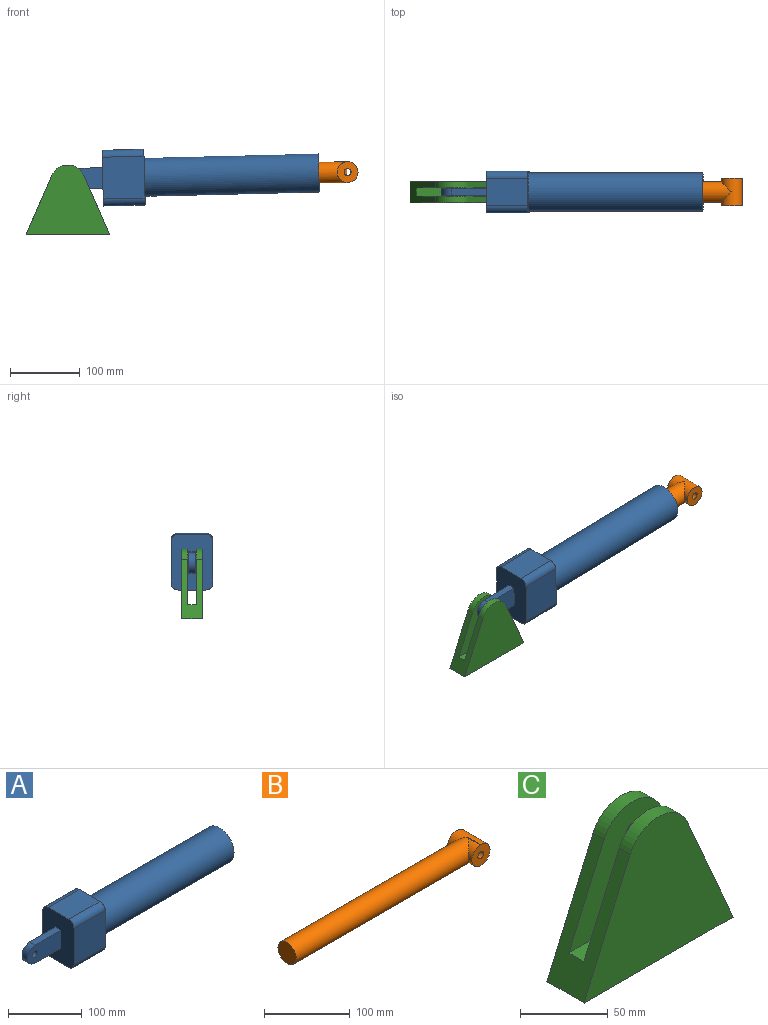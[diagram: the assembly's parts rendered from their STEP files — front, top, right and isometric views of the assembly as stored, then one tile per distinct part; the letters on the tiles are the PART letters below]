
ASSEMBLY  parts=3 mates=2
PART A: 20 faces, bbox 375x60x80 mm
  f0: cylinder r=27.5mm len=250mm, axis (1,0,0), area 43196.9mm2, adj f1,f13
  f1: plane 55x55mm, normal (1,0,0), area 1669mm2, adj f0,f2
  f2: cylinder r=15mm len=200mm, axis (1,0,0), area 18849.6mm2, adj f1,f3
  f3: plane 30x30mm, normal (1,0,0), area 706.9mm2, adj f2
  f4: plane 60x40mm, normal (0,0,1), area 2400mm2, adj f5,f11,f12,f13
  f5: cylinder r=10mm len=60mm, axis (1,0,0), area 942.5mm2, adj f4,f6,f12,f13
  f6: plane 60x60mm, normal (0,1,0), area 3600mm2, adj f5,f7,f12,f13
  f7: cylinder r=10mm len=60mm, axis (1,0,0), area 942.5mm2, adj f6,f8,f12,f13
  f8: plane 60x40mm, normal (0,0,-1), area 2400mm2, adj f7,f9,f12,f13
  f9: cylinder r=10mm len=60mm, axis (1,0,0), area 942.5mm2, adj f8,f10,f12,f13
  f10: plane 60x60mm, normal (0,-1,0), area 3600mm2, adj f9,f11,f12,f13
  f11: cylinder r=10mm len=60mm, axis (1,0,0), area 942.5mm2, adj f4,f10,f12,f13
  f12: plane 80x60mm, normal (-1,0,0), area 4414.2mm2, adj f4,f5,f6,f7,f8,f9,f10,f11
  f13: plane 80x60mm, normal (1,0,0), area 2338.3mm2, adj f0,f4,f5,f6,f7,f8,f9,f10
  f14: plane 50x10mm, normal (0,0,1), area 500mm2, adj f12,f16,f17,f19
  f15: plane 50x10mm, normal (0,0,-1), area 500mm2, adj f12,f16,f17,f19
  f16: plane 65x30mm, normal (0,-1,0), area 1774.9mm2, adj f12,f14,f15,f18,f19
  f17: plane 65x30mm, normal (0,1,0), area 1774.9mm2, adj f12,f14,f15,f18,f19
  f18: cylinder r=5mm len=10mm, axis (0,-1,0), area 314.2mm2, adj f16,f17
  f19: cylinder r=15mm len=30mm, axis (0,-1,0), area 471.2mm2, adj f14,f15,f16,f17
PART B: 6 faces, bbox 315x40x30 mm
  f0: cylinder r=15mm len=300mm, axis (-1,0,0), area 27374.3mm2, adj f1,f2
  f1: plane 30x30mm, normal (-1,0,0), area 706.9mm2, adj f0
  f2: cylinder r=15mm len=40mm, axis (0,1,0), area 2869.9mm2, adj f0,f3,f4
  f3: plane 30x30mm, normal (0,-1,0), area 628.3mm2, adj f2,f5
  f4: plane 30x30mm, normal (0,1,0), area 628.3mm2, adj f2,f5
  f5: cylinder r=5mm len=40mm, axis (0,-1,0), area 1256.6mm2, adj f3,f4
PART C: 11 faces, bbox 120x30x100 mm
  f0: cylinder r=25mm len=45.83mm, axis (0,1,0), area 521.7mm2, adj f1,f2,f6,f7
  f1: plane 85x37.09mm, normal (-0.92,0,0.4), area 1931.1mm2, adj f0,f3,f4,f5,f6,f7,f8,f9
  f2: plane 85x37.09mm, normal (0.92,0,0.4), area 1931.1mm2, adj f0,f3,f4,f5,f6,f7,f8,f9
  f3: cylinder r=25mm len=45.83mm, axis (0,1,0), area 521.7mm2, adj f1,f2,f5,f8
  f4: plane 120x30mm, normal (0,0,-1), area 3600mm2, adj f1,f2,f5,f6
  f5: plane 120x100mm, normal (0,-1,0), area 7543mm2, adj f1,f2,f3,f4
  f6: plane 120x100mm, normal (0,1,0), area 7543mm2, adj f0,f1,f2,f4
  f7: plane 102.55x80mm, normal (0,-1,0), area 5239mm2, adj f0,f1,f2,f9,f10
  f8: plane 102.55x80mm, normal (0,1,0), area 5239mm2, adj f1,f2,f3,f9,f10
  f9: plane 102.55x12mm, normal (0,0,1), area 1230.6mm2, adj f1,f2,f7,f8
  f10: cylinder r=5mm len=12mm, axis (0,-1,0), area 377mm2, adj f7,f8
PLACE A rot(axis=(0,-1,0),1.4deg) t=(178.37,-28.56,-88.2)mm
PLACE B rot(axis=(1,0,0.01),180deg) t=(69.64,-28.56,-90.87)mm
PLACE C t=(-181.52,-28.56,-97.05)mm fixed
MATE revolute C.f10 <-> A.f19  axis (0,-1,0) through (-181.52,-28.56,-97.05)mm
MATE slider B.f0 <-> A.f0  axis (-1,0,-0.02) through (-80.31,-28.56,-94.56)mm
